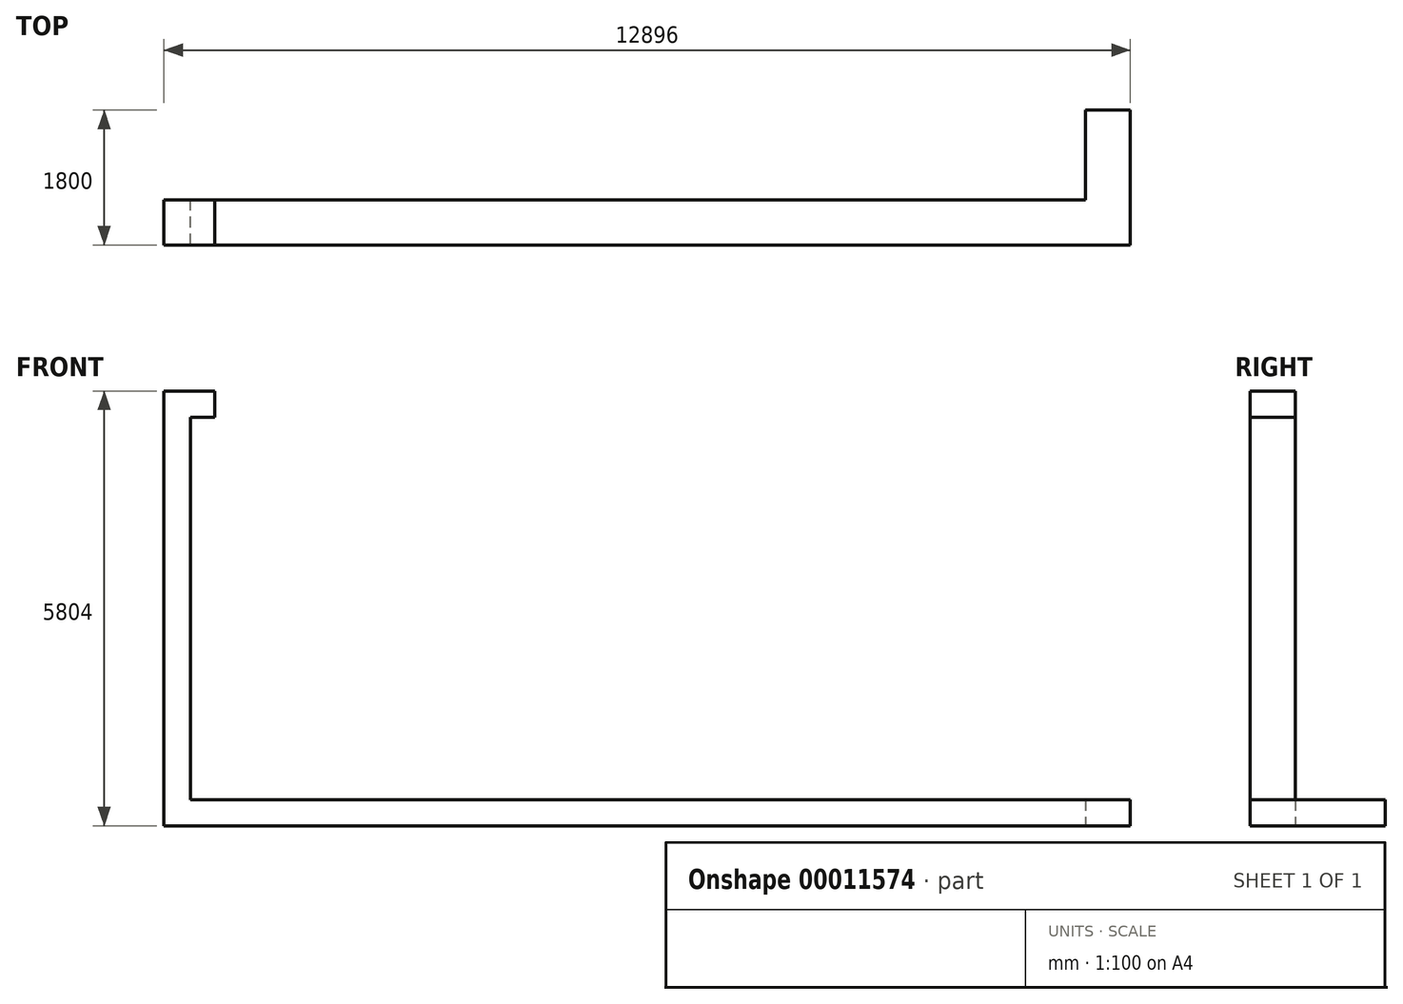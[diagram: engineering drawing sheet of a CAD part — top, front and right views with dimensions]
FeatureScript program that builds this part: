
annotation { "Feature Type Name" : "Feature", "Feature Type Description" : "" }
export const myFeature = defineFeature(function(context is Context, id is Id, definition is map)
    precondition{}
    {
        {
            var Q0;
            Q0=qCreatedBy(makeId("Front.planeOp"),FACE);
            var sketch = newSketch(context, id + "F0", { "sketchPlane" : qUnion([Q0])});
            skLineSegment(sketch, "E0", {"start": v(0, 0) * mm, "end": v(-500, 0) * mm});
            skLineSegment(sketch, "E1", {"start": v(-500, 0) * mm, "end": v(-500, -5454) * mm});
            skLineSegment(sketch, "E2", {"start": v(-500, -5454) * mm, "end": v(11921, -5454) * mm});
            skSolve(sketch);
        }
        {
            var Q0;
            Q0=qCreatedBy(makeId("Right.planeOp"),FACE);
            var sketch = newSketch(context, id + "F1", { "sketchPlane" : qUnion([Q0])});
            skLineSegment(sketch, "E3.rect.bottom", {"start": v(-300, 175) * mm, "end": v(300, 175) * mm});
            skLineSegment(sketch, "E3.rect.top", {"start": v(-300, -175) * mm, "end": v(300, -175) * mm});
            skLineSegment(sketch, "E3.rect.left", {"start": v(-300, 175) * mm, "end": v(-300, -175) * mm});
            skLineSegment(sketch, "E3.rect.right", {"start": v(300, 175) * mm, "end": v(300, -175) * mm});
            skPoint(sketch, "E3.rect.middle", {"position": v(0, 0) * mm});
            skSolve(sketch);
        }
        {
            var Q0;
            Q0=qCreatedBy(makeId("Top.planeOp"),FACE);
            cPlane(context, id + "F2", {"entities" : qUnion([Q0]), "cplaneType" : CPlaneType.OFFSET, "offset" : 5454 * mm, "oppositeDirection" : true, "width" : 150 * mm, "height" : 150 * mm});
        }
        {
            var Q0;
            Q0=qCreatedBy(id+"F2.planeOp",FACE);
            var sketch = newSketch(context, id + "F3", { "sketchPlane" : qUnion([Q0])});
            skLineSegment(sketch, "E4", {"start": v(11921, 0) * mm, "end": v(11921, 1500) * mm});
            skSolve(sketch);
        }
        {
            var Q0;
            Q0 = qSketchRegion(id + "F1", true);
            var Q1;
            Q1 = qBodyType(qCreatedBy(id + "F0" ,EDGE), BodyType.WIRE);
            var Q2;
            Q2=sQuery(id+"F3.wireOp",EDGE,"E4");
            sweep(context, id + "F4", {"profiles" : qUnion([Q0]), "path" : qUnion([Q1, Q2])});
        }
    });
